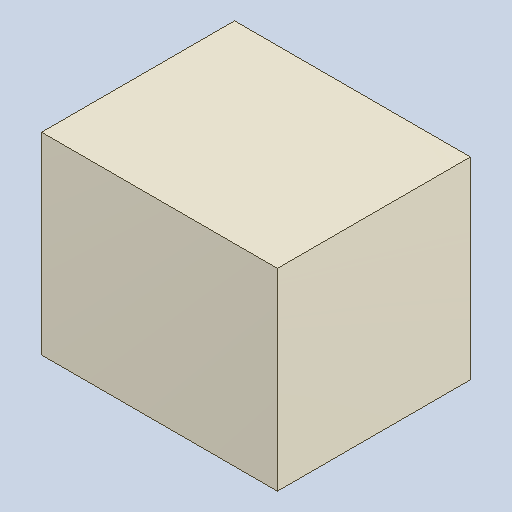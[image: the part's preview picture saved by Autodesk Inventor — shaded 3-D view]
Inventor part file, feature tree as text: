
AUTODESK INVENTOR PART (.ipt)
format: ipt  version: 2023.4 (Build 274418000, 418)  size: 81,920 bytes
history: native  units: mm
features: extrude x1
ambient origin geometry x8: Origin, YZ Plane, XZ Plane, XY Plane, X Axis, Y Axis, Z Axis, Center Point
bodies: Solid1 (feature_tree)
feature tree (1):
  extrude  "Extruded_10"  [1 undecoded]
note: 1 required parameter value undecoded (feature->parameter linkage not recoverable at this tier; creation-order binding heuristic only, values carry confidence <= 0.55)
